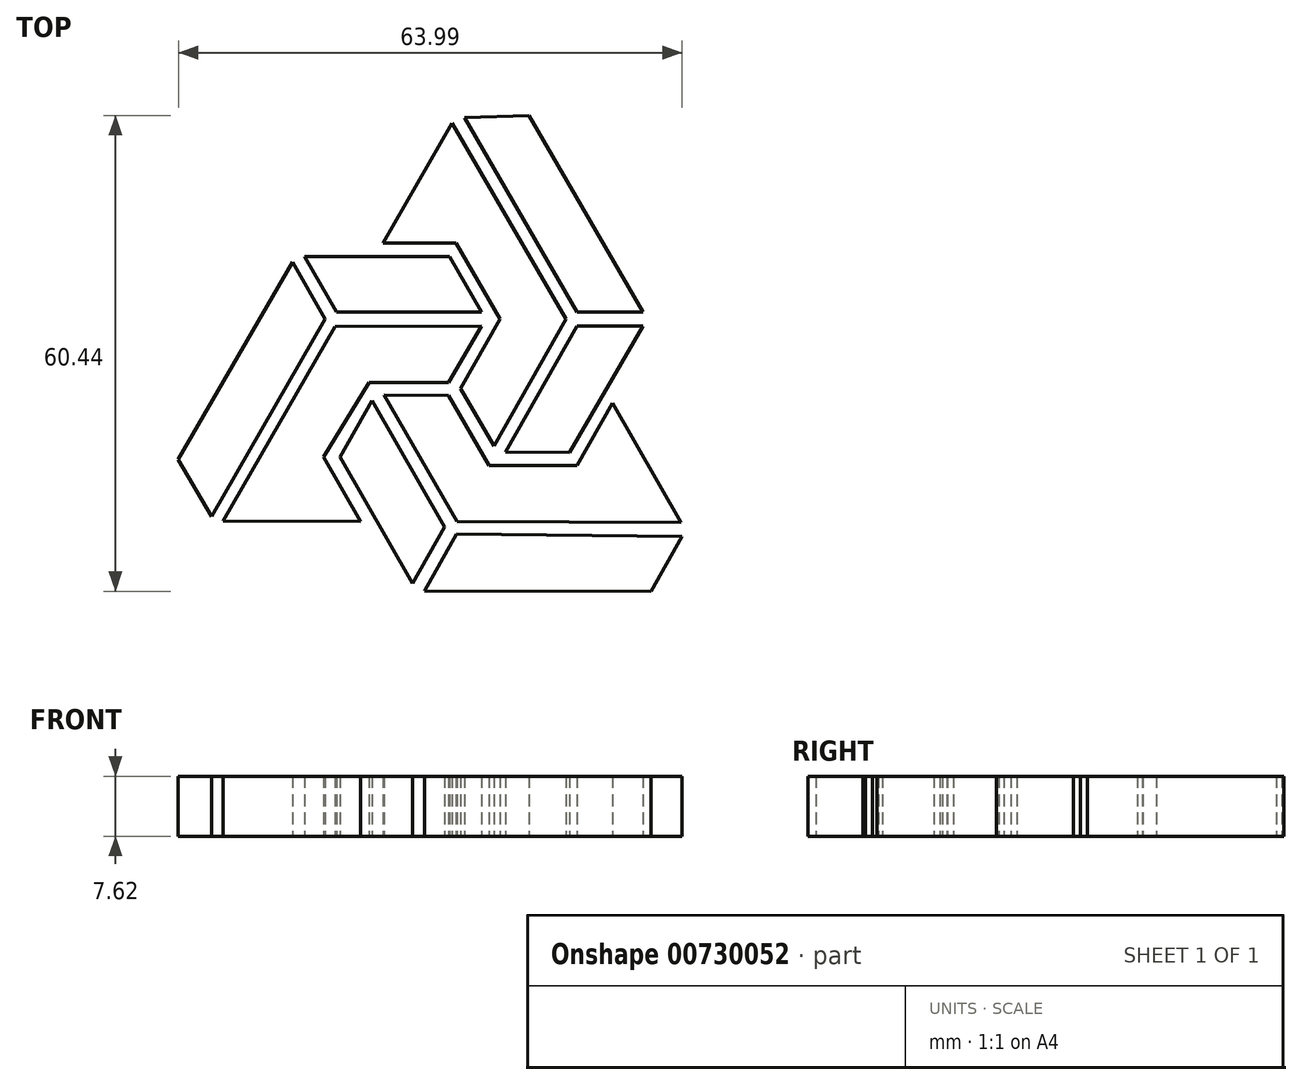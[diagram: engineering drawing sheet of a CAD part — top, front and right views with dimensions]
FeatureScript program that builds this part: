
annotation { "Feature Type Name" : "Feature", "Feature Type Description" : "" }
export const myFeature = defineFeature(function(context is Context, id is Id, definition is map)
    precondition{}
    {
        {
            var Q0;
            Q0=qCreatedBy(makeId("Top.planeOp"),FACE);
            var sketch = newSketch(context, id + "F0", { "sketchPlane" : qUnion([Q0])});
            skLineSegment(sketch, "E0", {"start": v(8.7, 32.67) * mm, "end": v(23.14, 7.73) * mm});
            skLineSegment(sketch, "E1", {"start": v(23.14, 7.73) * mm, "end": v(14.75, 7.73) * mm});
            skLineSegment(sketch, "E2", {"start": v(14.75, 7.73) * mm, "end": v(0.5, 32.4) * mm});
            skLineSegment(sketch, "E3", {"start": v(0.5, 32.4) * mm, "end": v(8.7, 32.67) * mm});
            skLineSegment(sketch, "E4", {"start": v(-1.06, 31.71) * mm, "end": v(-9.88, 16.5) * mm});
            skLineSegment(sketch, "E5", {"start": v(-9.88, 16.5) * mm, "end": v(-0.56, 16.5) * mm});
            skLineSegment(sketch, "E6", {"start": v(-0.56, 16.5) * mm, "end": v(5, 6.83) * mm});
            skLineSegment(sketch, "E7", {"start": v(5, 6.83) * mm, "end": v(0, -2) * mm});
            skLineSegment(sketch, "E8", {"start": v(0, -2) * mm, "end": v(4.22, -9.33) * mm});
            skLineSegment(sketch, "E9", {"start": v(4.22, -9.33) * mm, "end": v(13.38, 6.83) * mm});
            skLineSegment(sketch, "E10", {"start": v(13.38, 6.83) * mm, "end": v(-1.06, 31.71) * mm});
            skLineSegment(sketch, "E11", {"start": v(-19.82, 14.78) * mm, "end": v(-15.73, 7.73) * mm});
            skLineSegment(sketch, "E12", {"start": v(-15.73, 7.73) * mm, "end": v(2.67, 7.73) * mm});
            skLineSegment(sketch, "E13", {"start": v(2.67, 7.73) * mm, "end": v(-1.4, 14.73) * mm});
            skLineSegment(sketch, "E14", {"start": v(-1.4, 14.73) * mm, "end": v(-19.82, 14.78) * mm});
            skLineSegment(sketch, "E15", {"start": v(-21.34, 14.08) * mm, "end": v(-35.86, -11.01) * mm});
            skLineSegment(sketch, "E16", {"start": v(-35.86, -11.01) * mm, "end": v(-31.64, -18.29) * mm});
            skLineSegment(sketch, "E17", {"start": v(-31.64, -18.29) * mm, "end": v(-17.23, 6.83) * mm});
            skLineSegment(sketch, "E18", {"start": v(-17.23, 6.83) * mm, "end": v(-21.34, 14.08) * mm});
            skLineSegment(sketch, "E19", {"start": v(2.64, 5.93) * mm, "end": v(-1.52, -1.25) * mm});
            skLineSegment(sketch, "E20", {"start": v(-1.52, -1.25) * mm, "end": v(-11.66, -1.22) * mm});
            skLineSegment(sketch, "E21", {"start": v(-11.66, -1.22) * mm, "end": v(-17.4, -10.71) * mm});
            skLineSegment(sketch, "E22", {"start": v(-17.4, -10.71) * mm, "end": v(-12.7, -18.86) * mm});
            skLineSegment(sketch, "E23", {"start": v(-12.7, -18.86) * mm, "end": v(-30.17, -18.82) * mm});
            skLineSegment(sketch, "E24", {"start": v(-30.17, -18.82) * mm, "end": v(-15.95, 5.84) * mm});
            skLineSegment(sketch, "E25", {"start": v(-15.95, 5.84) * mm, "end": v(2.64, 5.93) * mm});
            skLineSegment(sketch, "E26", {"start": v(-9.75, -2.86) * mm, "end": v(-1.56, -2.88) * mm});
            skLineSegment(sketch, "E27", {"start": v(-1.56, -2.88) * mm, "end": v(3.6, -11.77) * mm});
            skLineSegment(sketch, "E28", {"start": v(3.6, -11.77) * mm, "end": v(14.78, -11.8) * mm});
            skLineSegment(sketch, "E29", {"start": v(14.78, -11.8) * mm, "end": v(19.28, -3.85) * mm});
            skLineSegment(sketch, "E30", {"start": v(19.28, -3.85) * mm, "end": v(28, -18.99) * mm});
            skLineSegment(sketch, "E31", {"start": v(28, -18.99) * mm, "end": v(-0.46, -18.92) * mm});
            skLineSegment(sketch, "E32", {"start": v(-0.46, -18.92) * mm, "end": v(-9.75, -2.86) * mm});
            skLineSegment(sketch, "E33", {"start": v(-11.28, -3.54) * mm, "end": v(-15.35, -10.71) * mm});
            skLineSegment(sketch, "E34", {"start": v(-15.35, -10.71) * mm, "end": v(-6.1, -26.76) * mm});
            skLineSegment(sketch, "E35", {"start": v(-6.1, -26.76) * mm, "end": v(-2.06, -19.6) * mm});
            skLineSegment(sketch, "E36", {"start": v(-2.06, -19.6) * mm, "end": v(-11.28, -3.54) * mm});
            skLineSegment(sketch, "E37", {"start": v(-0.5, -20.48) * mm, "end": v(-4.59, -27.7) * mm});
            skLineSegment(sketch, "E38", {"start": v(-4.59, -27.7) * mm, "end": v(24.16, -27.77) * mm});
            skLineSegment(sketch, "E39", {"start": v(24.16, -27.77) * mm, "end": v(28.13, -20.77) * mm});
            skLineSegment(sketch, "E40", {"start": v(28.13, -20.77) * mm, "end": v(-0.5, -20.48) * mm});
            skLineSegment(sketch, "E41", {"start": v(14.78, 5.93) * mm, "end": v(5.71, -10.09) * mm});
            skLineSegment(sketch, "E42", {"start": v(5.71, -10.09) * mm, "end": v(13.85, -10.1) * mm});
            skLineSegment(sketch, "E43", {"start": v(13.85, -10.1) * mm, "end": v(23.14, 5.93) * mm});
            skLineSegment(sketch, "E44", {"start": v(23.14, 5.93) * mm, "end": v(14.78, 5.93) * mm});
            skSolve(sketch);
        }
        {
            var Q0;
            Q0 = qSketchRegion(id + "F0", true);
            extrude(context, id + "F1", {"entities" : qUnion([Q0]), "depth" : 7.62 * mm, "offsetDistance" : 25.4 * mm});
        }
    });
